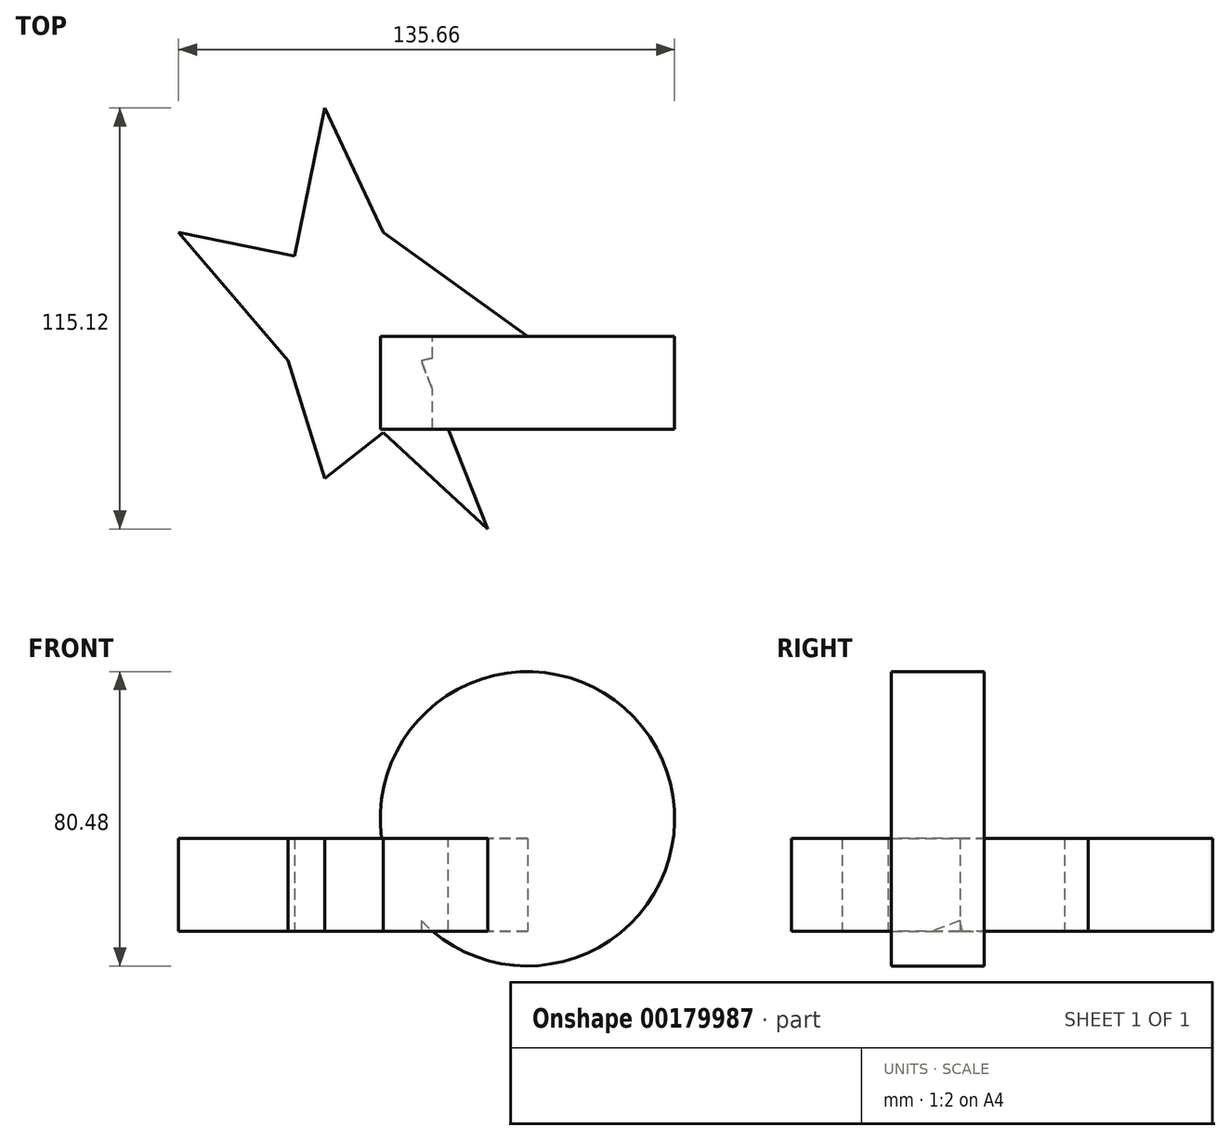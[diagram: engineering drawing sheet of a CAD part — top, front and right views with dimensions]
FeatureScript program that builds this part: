
annotation { "Feature Type Name" : "Feature", "Feature Type Description" : "" }
export const myFeature = defineFeature(function(context is Context, id is Id, definition is map)
    precondition{}
    {
        {
            var Q0;
            Q0=qCreatedBy(makeId("Top.planeOp"),FACE);
            var sketch = newSketch(context, id + "F0", { "sketchPlane" : qUnion([Q0])});
            skLineSegment(sketch, "E0", {"start": v(-55.41, 62.4) * mm, "end": v(-63.67, 21.91) * mm});
            skLineSegment(sketch, "E1", {"start": v(-63.67, 21.91) * mm, "end": v(-95.42, 28.4) * mm});
            skLineSegment(sketch, "E2", {"start": v(-95.42, 28.4) * mm, "end": v(-65.52, -6.7) * mm});
            skLineSegment(sketch, "E3", {"start": v(-65.52, -6.7) * mm, "end": v(-55.41, -38.88) * mm});
            skLineSegment(sketch, "E4", {"start": v(-55.41, -38.88) * mm, "end": v(-39.4, -26.32) * mm});
            skLineSegment(sketch, "E5", {"start": v(-39.4, -26.32) * mm, "end": v(-10.9, -52.72) * mm});
            skLineSegment(sketch, "E6", {"start": v(-10.9, -52.72) * mm, "end": v(-29.07, -6.7) * mm});
            skLineSegment(sketch, "E7", {"start": v(-29.07, -6.7) * mm, "end": v(0, 0) * mm});
            skLineSegment(sketch, "E8", {"start": v(0, 0) * mm, "end": v(-39.4, 28.4) * mm});
            skLineSegment(sketch, "E9", {"start": v(-39.4, 28.4) * mm, "end": v(-55.41, 62.4) * mm});
            skSolve(sketch);
        }
        {
            var Q0;
            Q0=makeQuery(id+"F0.imprint","IMPRINT",FACE,{"disambiguationData":[TD([[makeQuery(id+"F0.imprint","IMPRINT",EDGE,{"derivedFrom":sQuery(id+"F0.wireOp",EDGE,"E0")}),1.0]])]});
            extrude(context, id + "F1", {"entities" : qUnion([Q0]), "depth" : 25.4 * mm});
        }
        {
            var Q0;
            Q0=qCreatedBy(makeId("Front.planeOp"),FACE);
            var sketch = newSketch(context, id + "F2", { "sketchPlane" : qUnion([Q0])});
            skCircle(sketch, "E10", {"center": v(0, 30.72) * mm, "radius": 40.24 * mm});
            skSolve(sketch);
        }
        {
            var Q0;
            Q0=makeQuery(id+"F2.imprint","IMPRINT",FACE,{"disambiguationData":[TD([[makeQuery(id+"F2.imprint","IMPRINT",EDGE,{"derivedFrom":sQuery(id+"F2.wireOp",EDGE,"E10")}),1.0]])]});
            extrude(context, id + "F3", {"entities" : qUnion([Q0]), "operationType" : NewBodyOperationType.ADD, "depth" : 25.4 * mm});
        }
    });
